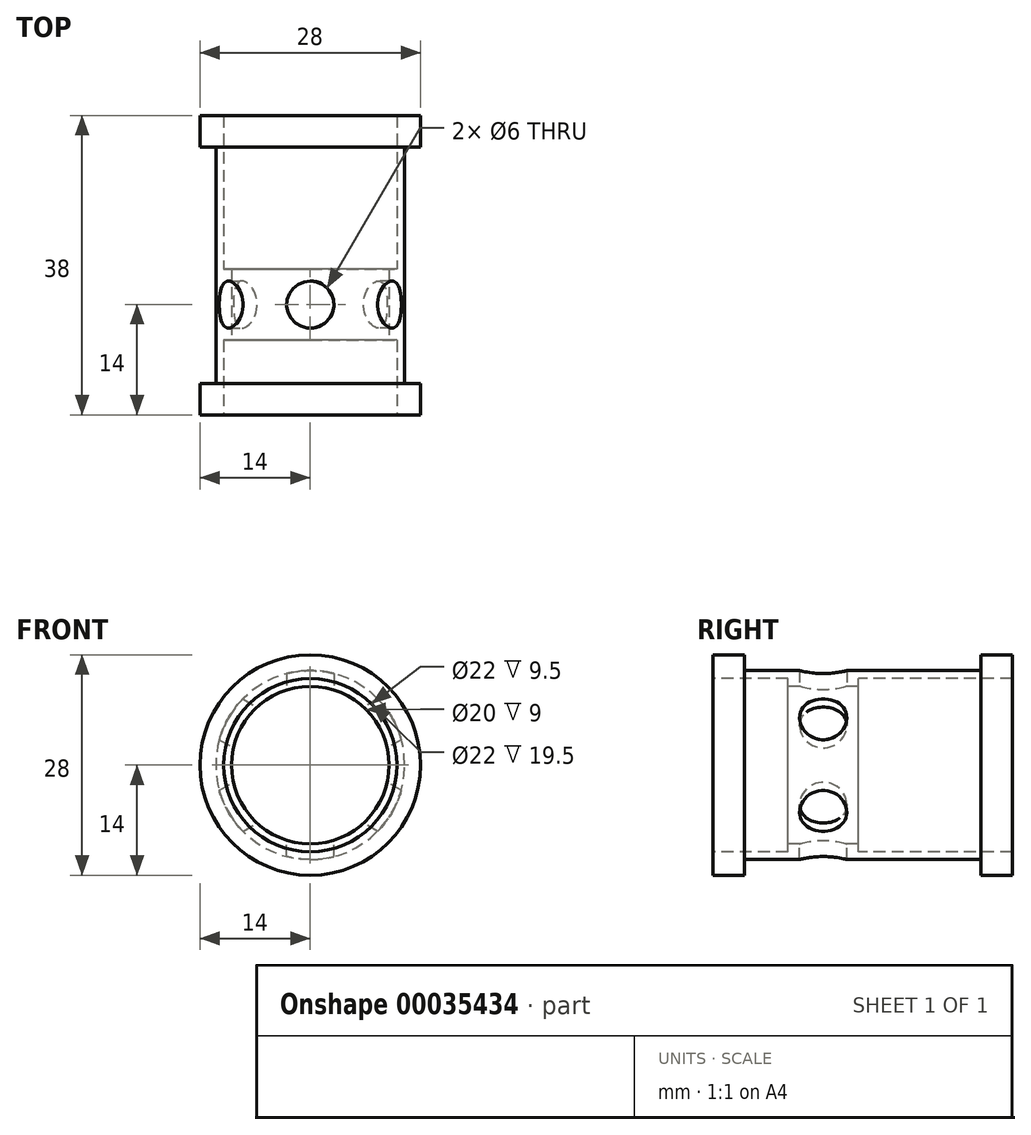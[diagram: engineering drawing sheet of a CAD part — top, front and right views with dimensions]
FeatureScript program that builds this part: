
annotation { "Feature Type Name" : "Feature", "Feature Type Description" : "" }
export const myFeature = defineFeature(function(context is Context, id is Id, definition is map)
    precondition{}
    {
        {
            var Q0;
            Q0=qCreatedBy(makeId("Right.planeOp"),FACE);
            var sketch = newSketch(context, id + "F0", { "sketchPlane" : qUnion([Q0])});
            skLineSegment(sketch, "E0", {"start": v(-19, 14) * mm, "end": v(-19, 11) * mm});
            skLineSegment(sketch, "E1", {"start": v(-19, 14) * mm, "end": v(-15, 14) * mm});
            skLineSegment(sketch, "E2", {"start": v(-15, 14) * mm, "end": v(-15, 12) * mm});
            skLineSegment(sketch, "E3", {"start": v(-15, 12) * mm, "end": v(15, 12) * mm});
            skLineSegment(sketch, "E4", {"start": v(15, 12) * mm, "end": v(15, 14) * mm});
            skLineSegment(sketch, "E5", {"start": v(15, 14) * mm, "end": v(19, 14) * mm});
            skLineSegment(sketch, "E6", {"start": v(19, 14) * mm, "end": v(19, 11) * mm});
            skLineSegment(sketch, "E7", {"start": v(-19, 0) * mm, "end": v(19, 0) * mm, "construction": true});
            skLineSegment(sketch, "E8", {"start": v(-19, 11) * mm, "end": v(-9.5, 11) * mm});
            skLineSegment(sketch, "E9", {"start": v(-9.5, 11) * mm, "end": v(-9.5, 10) * mm});
            skLineSegment(sketch, "E10", {"start": v(-9.5, 10) * mm, "end": v(-0.5, 10) * mm});
            skLineSegment(sketch, "E11", {"start": v(-0.5, 10) * mm, "end": v(-0.5, 11) * mm});
            skLineSegment(sketch, "E12", {"start": v(-0.5, 11) * mm, "end": v(19, 11) * mm});
            skLineSegment(sketch, "E13", {"start": v(-5, 10) * mm, "end": v(-5, 12) * mm, "construction": true});
            skLineSegment(sketch, "E14", {"start": v(0, 12) * mm, "end": v(0, 0) * mm, "construction": true});
            skSolve(sketch);
        }
        {
            var Q0;
            Q0=makeQuery(id+"F0.imprint","IMPRINT",FACE,{"disambiguationData":[TD([[makeQuery(id+"F0.imprint","IMPRINT",EDGE,{"derivedFrom":sQuery(id+"F0.wireOp",EDGE,"E0")}),1.0]])]});
            var Q1;
            Q1=sQuery(id+"F0.wireOp",EDGE,"E7");
            revolve(context, id + "F1", {"entities" : qUnion([Q0]), "axis" : qUnion([Q1]), "revolveType" : RevolveType.FULL});
        }
        {
            var Q0;
            Q0=qCreatedBy(makeId("Top.planeOp"),FACE);
            var sketch = newSketch(context, id + "F2", { "sketchPlane" : qUnion([Q0])});
            skCircle(sketch, "E15", {"center": v(0, -5) * mm, "radius": 3 * mm});
            skSolve(sketch);
        }
        {
            var Q0;
            Q0 = qSketchRegion(id + "F2", true);
            extrude(context, id + "F3", {"entities" : qUnion([Q0]), "operationType" : NewBodyOperationType.REMOVE, "oppositeDirection" : true, "depth" : 25.4 * mm});
        }
        {
            var Q0;
            Q0=makeQuery(id+"F3.boolean.opBoolean","COPY",FACE,{"derivedFrom":makeQuery(id+"F3.opExtrude","SWEPT_FACE",FACE,{"disambiguationData":[OSD([sQuery(id+"F2.wireOp",EDGE,"E15")])]})});
            var Q1;
            Q1=makeQuery(id+"F1.opRevolve","SWEPT_FACE",FACE,{"disambiguationData":[OSD([sQuery(id+"F0.wireOp",EDGE,"E8")])]});
            circularPattern(context, id + "F4", {"faces" : qUnion([Q0]), "axis" : qUnion([Q1]), "angle" : 360 * degree, "instanceCount" : 6, "equalSpace" : true, "patternType" : PatternType.FACE});
        }
    });
